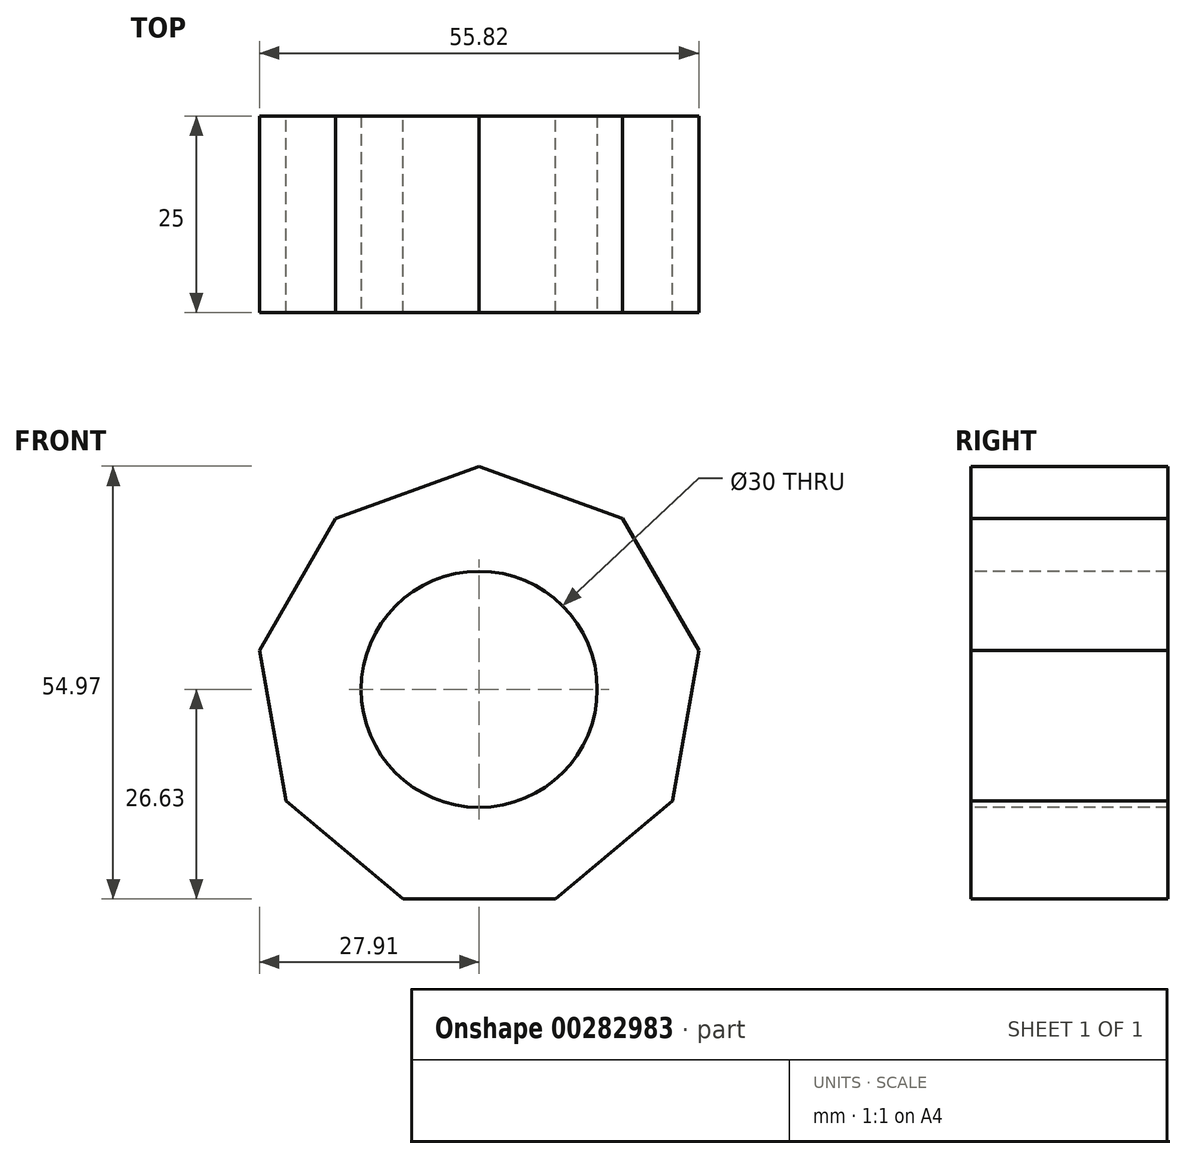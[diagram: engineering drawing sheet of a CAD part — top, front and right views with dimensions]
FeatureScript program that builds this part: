
annotation { "Feature Type Name" : "Feature", "Feature Type Description" : "" }
export const myFeature = defineFeature(function(context is Context, id is Id, definition is map)
    precondition{}
    {
        {
            var Q0;
            Q0=qCreatedBy(makeId("Front.planeOp"),FACE);
            var sketch = newSketch(context, id + "F0", { "sketchPlane" : qUnion([Q0])});
            skCircle(sketch, "E0.cCircle", {"center": v(0, 0) * mm, "radius": 26.63 * mm, "construction": true});
            skLineSegment(sketch, "E0.0", {"start": v(9.7, -26.63) * mm, "end": v(-9.7, -26.63) * mm});
            skLineSegment(sketch, "E0.1", {"start": v(-9.7, -26.63) * mm, "end": v(-24.54, -14.17) * mm});
            skLineSegment(sketch, "E0.2", {"start": v(-24.54, -14.17) * mm, "end": v(-27.9, 4.92) * mm});
            skLineSegment(sketch, "E0.3", {"start": v(-27.9, 4.92) * mm, "end": v(-18.21, 21.7) * mm});
            skLineSegment(sketch, "E0.4", {"start": v(-18.21, 21.7) * mm, "end": v(0, 28.34) * mm});
            skLineSegment(sketch, "E0.5", {"start": v(0, 28.34) * mm, "end": v(18.21, 21.7) * mm});
            skLineSegment(sketch, "E0.6", {"start": v(18.21, 21.7) * mm, "end": v(27.9, 4.92) * mm});
            skLineSegment(sketch, "E0.7", {"start": v(27.9, 4.92) * mm, "end": v(24.54, -14.17) * mm});
            skLineSegment(sketch, "E0.8", {"start": v(24.54, -14.17) * mm, "end": v(9.7, -26.63) * mm});
            skPoint(sketch, "E0.0.midPoint", {"position": v(0, -26.63) * mm});
            skSolve(sketch);
        }
        {
            var Q0;
            Q0 = qSketchRegion(id + "F0", true);
            extrude(context, id + "F1", {"entities" : qUnion([Q0]), "depth" : 25 * mm});
        }
        {
            var Q0;
            Q0=makeQuery(id+"F1.opExtrude","CAP_FACE",FACE,{"disambiguationData":[OSD([sQuery(id+"F0.wireOp",EDGE,"E0.0"),sQuery(id+"F0.wireOp",EDGE,"E0.1"),sQuery(id+"F0.wireOp",EDGE,"E0.2"),sQuery(id+"F0.wireOp",EDGE,"E0.3"),sQuery(id+"F0.wireOp",EDGE,"E0.4"),sQuery(id+"F0.wireOp",EDGE,"E0.5"),sQuery(id+"F0.wireOp",EDGE,"E0.6"),sQuery(id+"F0.wireOp",EDGE,"E0.7"),sQuery(id+"F0.wireOp",EDGE,"E0.8")])],"isStart":false});
            var sketch = newSketch(context, id + "F2", { "sketchPlane" : qUnion([Q0])});
            skCircle(sketch, "E1", {"center": v(0, 0) * mm, "radius": 15 * mm});
            skSolve(sketch);
        }
        {
            var Q0;
            Q0 = qSketchRegion(id + "F2", true);
            extrude(context, id + "F3", {"entities" : qUnion([Q0]), "operationType" : NewBodyOperationType.REMOVE, "oppositeDirection" : true, "depth" : 44.4 * mm});
        }
    });
